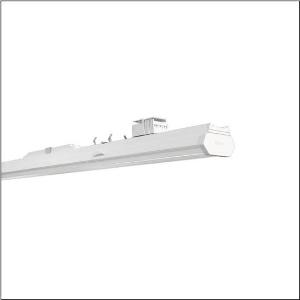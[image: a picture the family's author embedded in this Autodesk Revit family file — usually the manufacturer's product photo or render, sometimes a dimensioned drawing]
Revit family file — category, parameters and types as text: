
# Revit family: licross_11_protected_mo_51tp12cn49xg
name_source: partatom
category: Lighting Fixtures
units: mm (PartAtom-declared; Revit-internal decimal feet)

## family parameters
Cut with Voids When Loaded = No
Host = Face
Light Source = No
Part Type = Normal
Room Calculation Point = No
Round Connector Dimension = Use Diameter
Shared = No

## types (1)
- --- (1 x LED, 9070 lm, 49.4 W, 4000K)
    Apparent Load = 49 VA
    CIE Flux Codes = 73 92 98 99 100
    Color Rendering = 80
    Color Temperature = 4000K
    Default Elevation = 1800 mm
    Description = Licross 11 Protected MO, luminaire insert, of sheet steel, galvanised, coil coated, white, length: 1.500mm, width: 90mm, height: 101mm, LED rated luminous flux: 9.070lm, light colour: 840, SDCM (Standard Deviation of Colour Matching)MacAdam ≤ 2 SDCM (initial), control gear: ON/OFF Multilumen, CLOi, with plug, 3-pole, with phase selection, mains connection: 220..240V, AC, 50/60Hz, start of lifetime: 49W, end of service life: 55W, internal wiring halogen-free, primary light control with lens, of plastic, primary optical cover: cover, of PMMA, light emission: direct distribution, primary light characteristic: symmetric, protection rating (complete): IP64, insulation class (complete): insulation class I (protective earthing), certification: CE, ENEC, VDE, UKCA, protection symbol: D if used in an environment with conductive dust loads with corresponding accessories, impact resistance: IK06, permissible ambient temperature for indoor applications: -35..+40°C, corresponds to IFS (International Featured Standards) requirements for safety and quality in the food industry, reducing of maximum allowable ambient temperature of 5°C with ceiling mounting, LABS conformity tested according to VDMA 24364:2018-05, The light source and the operating device comply with the requirements of the Ecodesign Regulation (EU) 2019/2020 and are replaceable in accordance with this regulation, packaging unit: 1 piece
    Height = 92 mm
    Lamp = 1 x LED
    Lamp Light Flux = 9070 lm
    Lamp Power = 49.4 W
    Lamp count = 1
    Length = 1500 mm
    Luminous efficacy = 184 lm/W
    Manufacturer = Siteco
    ModVariant = No
    Model = 51TP12CN49XG
    Mounting Place = Ceiling
    Mounting Type = Pendant
    Number of Poles = 1
    OnlyDefault = Yes
    Power Factor = 1
    Product Name = Licross 11 Protected MO
    Product group = luminaire insert | ceiling pendant
    ProductGroupID = 901
    Protection Class = Protection class I
    Protection Degree = IP 64
    RLX_Detail_Level = 1
    RLX_Emergency_Light_Flux = 0 lm
    RLX_Emergency_Type = 0
    RLX_Emergency_Type_DB = No
    RlxData = <blob elided: 22441 chars, md5=7170b780>
    Socket = socket
    Standby Power = 0 W
    System Light Flux = 9070 lm
    System Power = 49 W
    Type Comments = factory setting: luminous flux: 100 % | (A | C | E) | 113 mA
    Type Image = l_1256148.jpg
    URL = http://relux.com
    VarID = @adj_000831
    Voltage = 0 V
    Weight = 0.00 kg
    Width = 88 mm

## geometry (parser evidence)
native form markers: Blend x4, Sweep x9
no freeform markers — native parametric forms only
